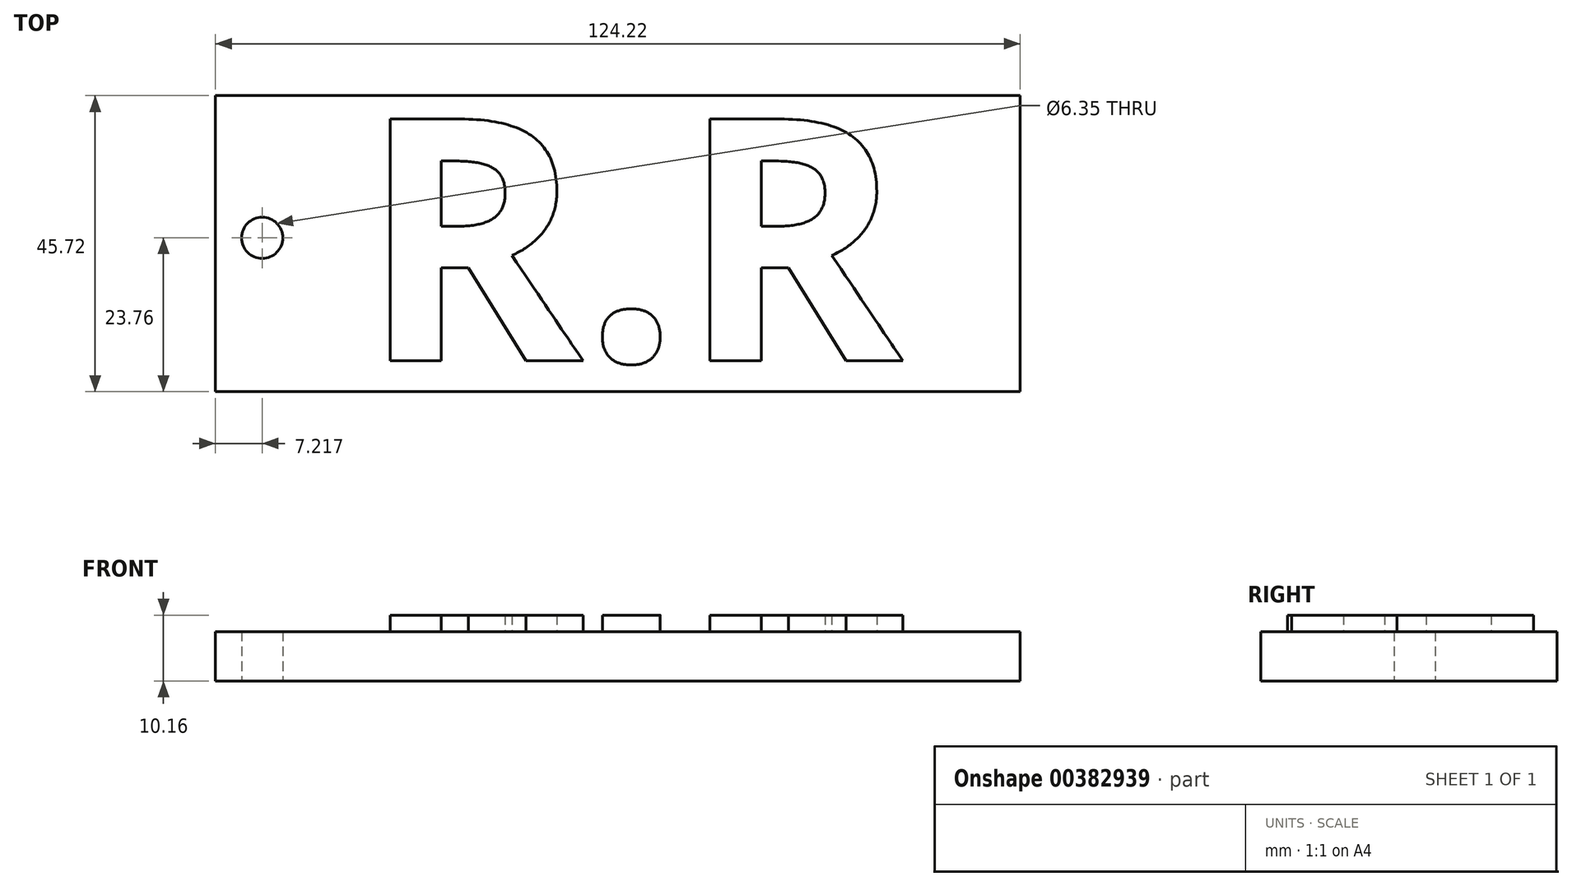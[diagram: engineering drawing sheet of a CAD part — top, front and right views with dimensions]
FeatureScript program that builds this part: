
annotation { "Feature Type Name" : "Feature", "Feature Type Description" : "" }
export const myFeature = defineFeature(function(context is Context, id is Id, definition is map)
    precondition{}
    {
        {
            var Q0;
            Q0=qCreatedBy(makeId("Top.planeOp"),FACE);
            var sketch = newSketch(context, id + "F0", { "sketchPlane" : qUnion([Q0])});
            skLineSegment(sketch, "E0.bottom", {"start": v(-61.66, 21.96) * mm, "end": v(62.56, 21.96) * mm});
            skLineSegment(sketch, "E0.top", {"start": v(-61.66, -23.76) * mm, "end": v(62.56, -23.76) * mm});
            skLineSegment(sketch, "E0.left", {"start": v(-61.66, 21.96) * mm, "end": v(-61.66, -23.76) * mm});
            skLineSegment(sketch, "E0.right", {"start": v(62.56, 21.96) * mm, "end": v(62.56, -23.76) * mm});
            skSolve(sketch);
        }
        {
            var Q0;
            Q0=qCreatedBy(makeId("Top.planeOp"),FACE);
            var sketch = newSketch(context, id + "F1", { "sketchPlane" : qUnion([Q0])});
            skCircle(sketch, "E1", {"center": v(-54.44, 0) * mm, "radius": 4.6 * mm});
            skSolve(sketch);
        }
        {
            var Q0;
            Q0 = qSketchRegion(id + "F0", true);
            extrude(context, id + "F2", {"entities" : qUnion([Q0]), "depth" : 7.62 * mm});
        }
        {
            var Q0;
            Q0=sQuery(id+"F1.wireOp",VERTEX,"E1.center");
            var Q1;
            Q1=makeQuery(id+"F2.opExtrude","SWEPT_BODY",BODY,{"disambiguationData":[OSD([sQuery(id+"F0.wireOp",EDGE,"E0.bottom"),sQuery(id+"F0.wireOp",EDGE,"E0.top"),sQuery(id+"F0.wireOp",EDGE,"E0.left"),sQuery(id+"F0.wireOp",EDGE,"E0.right")])]});
            hole(context, id + "F3", {"style" : HoleStyle.SIMPLE, "endStyle" : HoleEndStyle.THROUGH, "oppositeDirection" : true, "holeDiameter" : 6.35 * mm, "isTappedThrough" : true, "tappedDepth" : 12.7 * mm, "tapClearance" : 3, "locations" : qUnion([Q0]), "scope" : qUnion([Q1])});
        }
        {
            var Q0;
            Q0=makeQuery(id+"F2.opExtrude","CAP_FACE",FACE,{"disambiguationData":[OSD([sQuery(id+"F0.wireOp",EDGE,"E0.bottom"),sQuery(id+"F0.wireOp",EDGE,"E0.top"),sQuery(id+"F0.wireOp",EDGE,"E0.left"),sQuery(id+"F0.wireOp",EDGE,"E0.right")])],"isStart":false});
            var sketch = newSketch(context, id + "F4", { "sketchPlane" : qUnion([Q0])});
            skText(sketch, "E2", { "text": "R.R\n", "fontName": "OpenSans-Bold.ttf"});
            const initialGuessF4  = {"E2": [-0.0394, -0.01895, 1, 0, 0.0376]};
            skSetInitialGuess(sketch, initialGuessF4);
            skSolve(sketch);
        }
        {
            var Q0;
            Q0 = qSketchRegion(id + "F4", true);
            extrude(context, id + "F5", {"entities" : qUnion([Q0]), "operationType" : NewBodyOperationType.ADD, "depth" : 2.54 * mm});
        }
    });
